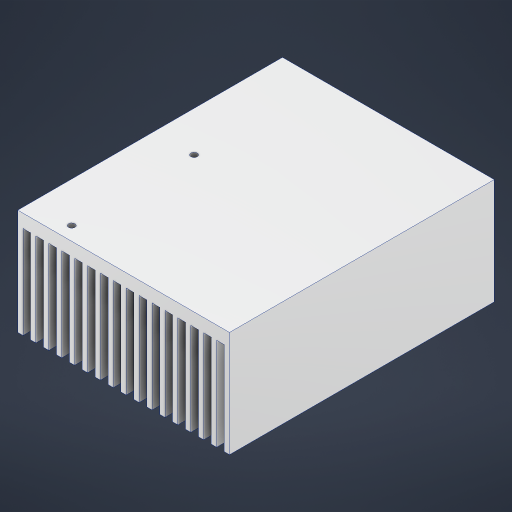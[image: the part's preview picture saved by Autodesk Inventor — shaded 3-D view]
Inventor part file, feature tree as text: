
AUTODESK INVENTOR PART (.ipt)
format: ipt  version: 2024.2 (Build 282272000, 272)  size: 267,264 bytes
history: native  units: in
note: dims shown in document units (in); Inventor stores cm internally (conversion verified against a paired STEP export)
features: extrude x1, hole x1
ambient origin geometry x8: Origin, YZ Plane, XZ Plane, XY Plane, X Axis, Y Axis, Z Axis, Center Point
bodies: Solid1 (feature_tree)
feature tree (2):
  extrude  "Extrusion1"  Depth=1.5748in
  hole  "Hole1"  [1 undecoded]
note: 1 required parameter value undecoded (feature->parameter linkage not recoverable at this tier; creation-order binding heuristic only, values carry confidence <= 0.55)
